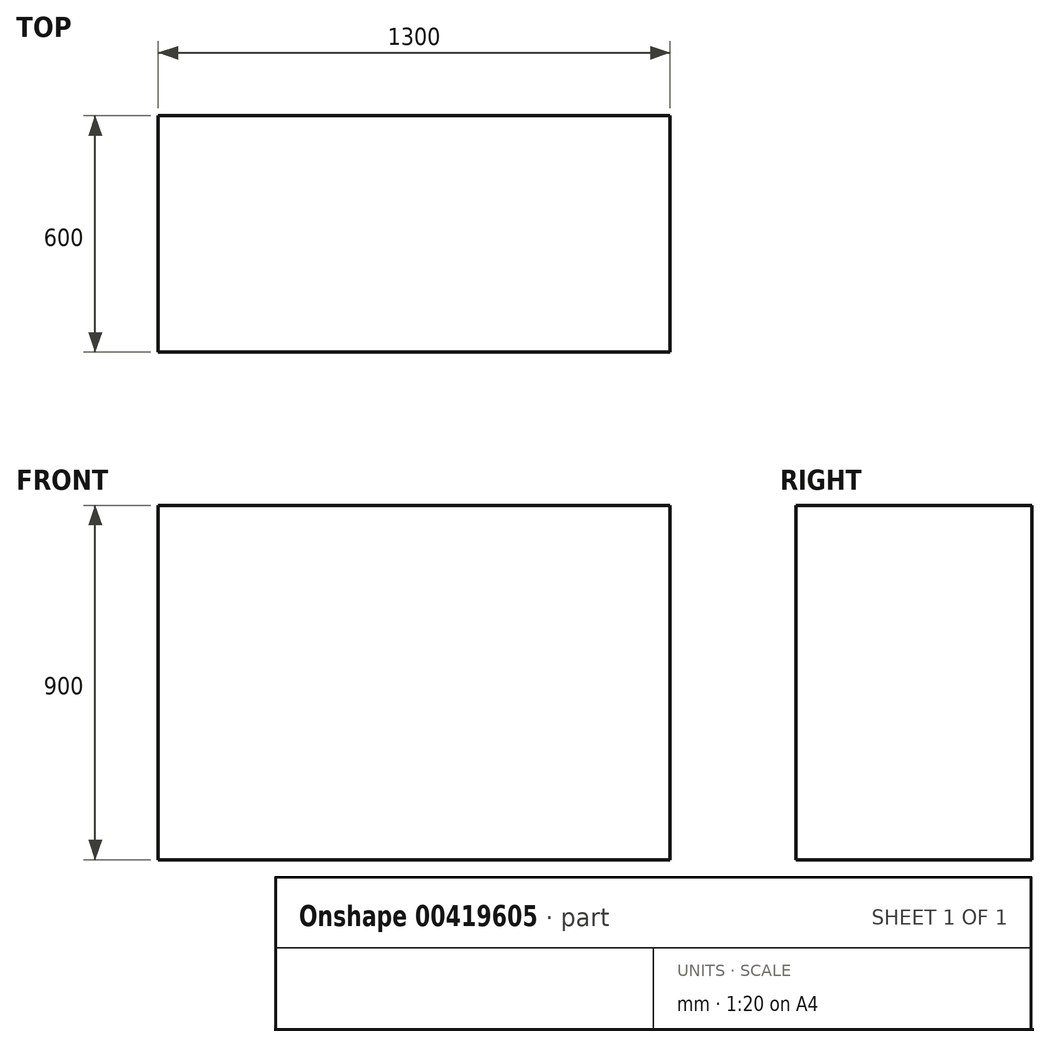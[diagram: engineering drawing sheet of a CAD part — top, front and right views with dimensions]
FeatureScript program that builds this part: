
annotation { "Feature Type Name" : "Feature", "Feature Type Description" : "" }
export const myFeature = defineFeature(function(context is Context, id is Id, definition is map)
    precondition{}
    {
        {
            var Q0;
            Q0=qCreatedBy(makeId("Top.planeOp"),FACE);
            var sketch = newSketch(context, id + "F0", { "sketchPlane" : qUnion([Q0])});
            skLineSegment(sketch, "E0.bottom", {"start": v(-1164.3, 541.1) * mm, "end": v(135.7, 541.1) * mm});
            skLineSegment(sketch, "E0.top", {"start": v(-1164.3, -58.9) * mm, "end": v(135.7, -58.9) * mm});
            skLineSegment(sketch, "E0.left", {"start": v(-1164.3, 541.1) * mm, "end": v(-1164.3, -58.9) * mm});
            skLineSegment(sketch, "E0.right", {"start": v(135.7, 541.1) * mm, "end": v(135.7, -58.9) * mm});
            skSolve(sketch);
        }
        {
            var Q0;
            Q0=makeQuery(id+"F0.imprint","IMPRINT",FACE,{"disambiguationData":[TD([[makeQuery(id+"F0.imprint","IMPRINT",EDGE,{"derivedFrom":sQuery(id+"F0.wireOp",EDGE,"E0.bottom")}),-1.0]])]});
            extrude(context, id + "F1", {"entities" : qUnion([Q0]), "depth" : 900 * mm});
        }
    });
